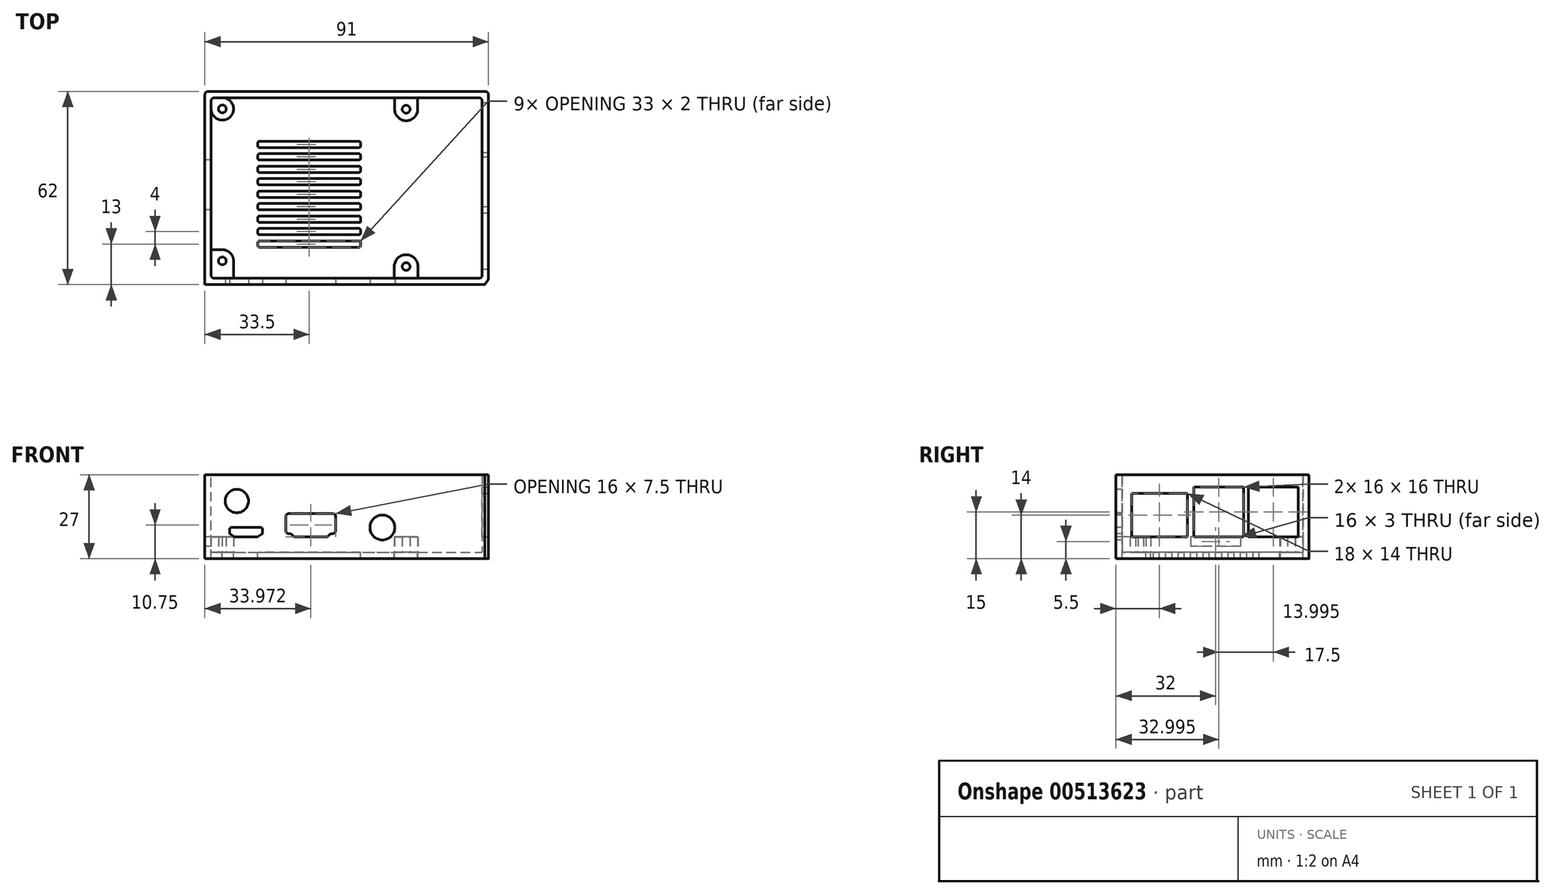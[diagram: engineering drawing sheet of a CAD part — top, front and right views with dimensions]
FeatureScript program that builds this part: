
annotation { "Feature Type Name" : "Feature", "Feature Type Description" : "" }
export const myFeature = defineFeature(function(context is Context, id is Id, definition is map)
    precondition{}
    {
        {
            var Q0;
            Q0=qCreatedBy(makeId("Top.planeOp"),FACE);
            var sketch = newSketch(context, id + "F0", { "sketchPlane" : qUnion([Q0])});
            skLineSegment(sketch, "E0.bottom", {"start": v(1, 0) * mm, "end": v(86, 0) * mm});
            skLineSegment(sketch, "E0.top", {"start": v(1, -58) * mm, "end": v(86, -58) * mm});
            skLineSegment(sketch, "E0.left", {"start": v(0, -1) * mm, "end": v(0, -57) * mm});
            skLineSegment(sketch, "E0.right", {"start": v(87, -1) * mm, "end": v(87, -57) * mm});
            skLineSegment(sketch, "E1.0", {"start": v(0, 2) * mm, "end": v(87, 2) * mm});
            skLineSegment(sketch, "E2.0", {"start": v(-2, -60) * mm, "end": v(87.8, -60) * mm});
            skLineSegment(sketch, "E3.0", {"start": v(89, 0) * mm, "end": v(89, -56.4) * mm});
            skLineSegment(sketch, "E4.0", {"start": v(-2, 0) * mm, "end": v(-2, -56) * mm});
            skLineSegment(sketch, "E5", {"start": v(0, 2) * mm, "end": v(-1, 2) * mm});
            skLineSegment(sketch, "E6", {"start": v(-2, 1) * mm, "end": v(-2, 0) * mm});
            skLineSegment(sketch, "E7", {"start": v(-2, -58) * mm, "end": v(-2, -56) * mm});
            skLineSegment(sketch, "E8", {"start": v(-2, -60) * mm, "end": v(-2, -58) * mm});
            skPoint(sketch, "E9.visualSharp", {"position": v(-2, 2) * mm});
            skArc(sketch, "E9.filletArc", {"start": v(-1, 2) * mm, "mid": v(-1.7, 1.7) * mm, "end": v(-2, 1) * mm});
            skPoint(sketch, "E10.visualSharp", {"position": v(0, 0) * mm});
            skArc(sketch, "E10.filletArc", {"start": v(1, 0) * mm, "mid": v(0.3, -0.3) * mm, "end": v(0, -1) * mm});
            skPoint(sketch, "E11.visualSharp", {"position": v(-2, -58) * mm});
            skPoint(sketch, "E12.visualSharp", {"position": v(0, -58) * mm});
            skArc(sketch, "E12.filletArc", {"start": v(0, -57) * mm, "mid": v(0.3, -57.7) * mm, "end": v(1, -58) * mm});
            skPoint(sketch, "E13.visualSharp", {"position": v(87, -58) * mm});
            skArc(sketch, "E13.filletArc", {"start": v(86, -58) * mm, "mid": v(86.7, -57.7) * mm, "end": v(87, -57) * mm});
            skPoint(sketch, "E14.visualSharp", {"position": v(87, 0) * mm});
            skArc(sketch, "E14.filletArc", {"start": v(87, -1) * mm, "mid": v(86.7, -0.3) * mm, "end": v(86, 0) * mm});
            skLineSegment(sketch, "E15", {"start": v(89, -56.4) * mm, "end": v(89, -58.06) * mm});
            skLineSegment(sketch, "E16", {"start": v(87.8, -60) * mm, "end": v(88.8, -58.66) * mm});
            skLineSegment(sketch, "E17", {"start": v(89, 0) * mm, "end": v(89, 1) * mm});
            skLineSegment(sketch, "E18", {"start": v(88, 2) * mm, "end": v(87, 2) * mm});
            skPoint(sketch, "E19.visualSharp", {"position": v(89, 2) * mm});
            skArc(sketch, "E19.filletArc", {"start": v(89, 1) * mm, "mid": v(88.7, 1.7) * mm, "end": v(88, 2) * mm});
            skPoint(sketch, "E20.visualSharp", {"position": v(89, -58.4) * mm});
            skArc(sketch, "E20.filletArc", {"start": v(88.8, -58.66) * mm, "mid": v(88.95, -58.38) * mm, "end": v(89, -58.06) * mm});
            skLineSegment(sketch, "E21.bottom", {"start": v(0, 0) * mm, "end": v(3.6, 0) * mm, "construction": true});
            skLineSegment(sketch, "E21.left", {"start": v(0, 0) * mm, "end": v(0, -3.6) * mm, "construction": true});
            skArc(sketch, "E22", {"start": v(0, -3.6) * mm, "mid": v(6.15, -6.15) * mm, "end": v(3.6, 0) * mm});
            skCircle(sketch, "E23", {"center": v(3.6, -3.6) * mm, "radius": 1.25 * mm});
            skLineSegment(sketch, "E24.bottom", {"start": v(0, -58) * mm, "end": v(3.6, -58) * mm, "construction": true});
            skLineSegment(sketch, "E24.left", {"start": v(0, -58) * mm, "end": v(0, -54.4) * mm, "construction": true});
            skLineSegment(sketch, "E25.bottom", {"start": v(15.5, -48) * mm, "end": v(47.5, -48) * mm});
            skLineSegment(sketch, "E25.top", {"start": v(15, -46) * mm, "end": v(48, -46) * mm});
            skLineSegment(sketch, "E25.left", {"start": v(15, -47.5) * mm, "end": v(15, -46.5) * mm});
            skLineSegment(sketch, "E25.right", {"start": v(48, -47.5) * mm, "end": v(48, -46.5) * mm});
            skLineSegment(sketch, "E26.bottom", {"start": v(15.5, -46) * mm, "end": v(47.5, -46) * mm});
            skLineSegment(sketch, "E26.top", {"start": v(15, -44) * mm, "end": v(48, -44) * mm});
            skLineSegment(sketch, "E27.direction1", {"start": v(15.5, -44) * mm, "end": v(40, -44) * mm, "construction": true});
            skLineSegment(sketch, "E28.bottom", {"start": v(15, -44) * mm, "end": v(47.5, -44) * mm});
            skLineSegment(sketch, "E28.top", {"start": v(15.5, -42) * mm, "end": v(47.5, -42) * mm});
            skLineSegment(sketch, "E28.left", {"start": v(15, -43.5) * mm, "end": v(15, -42.5) * mm});
            skLineSegment(sketch, "E29.bottom", {"start": v(48, -42) * mm, "end": v(15, -42) * mm});
            skLineSegment(sketch, "E29.top", {"start": v(48, -40) * mm, "end": v(15, -40) * mm});
            skLineSegment(sketch, "E30.bottom", {"start": v(15.5, -40) * mm, "end": v(47.5, -40) * mm});
            skLineSegment(sketch, "E30.top", {"start": v(15.5, -38) * mm, "end": v(47.5, -38) * mm});
            skLineSegment(sketch, "E30.left", {"start": v(15, -39.5) * mm, "end": v(15, -38.5) * mm});
            skLineSegment(sketch, "E30.right", {"start": v(48, -40) * mm, "end": v(48, -38.5) * mm});
            skLineSegment(sketch, "E31.1.0.0", {"start": v(15.5, -36) * mm, "end": v(47.5, -36) * mm});
            skLineSegment(sketch, "E31.2.0.0", {"start": v(15.5, -34) * mm, "end": v(47.5, -34) * mm});
            skLineSegment(sketch, "E31.3.0.0", {"start": v(15.5, -32) * mm, "end": v(47.5, -32) * mm});
            skLineSegment(sketch, "E31.4.0.0", {"start": v(15.5, -30) * mm, "end": v(47.5, -30) * mm});
            skLineSegment(sketch, "E31.5.0.0", {"start": v(15.5, -28) * mm, "end": v(47.5, -28) * mm});
            skLineSegment(sketch, "E31.6.0.0", {"start": v(15.5, -26) * mm, "end": v(47.5, -26) * mm});
            skLineSegment(sketch, "E31.7.0.0", {"start": v(15.5, -24) * mm, "end": v(47.5, -24) * mm});
            skLineSegment(sketch, "E31.8.0.0", {"start": v(15.5, -22) * mm, "end": v(47.5, -22) * mm});
            skLineSegment(sketch, "E31.9.0.0", {"start": v(15.5, -20) * mm, "end": v(47.5, -20) * mm});
            skLineSegment(sketch, "E31.10.0.0", {"start": v(15.5, -18) * mm, "end": v(47.5, -18) * mm});
            skLineSegment(sketch, "E31.11.0.0", {"start": v(15.5, -16) * mm, "end": v(47.5, -16) * mm});
            skLineSegment(sketch, "E31.12.0.0", {"start": v(15.5, -14) * mm, "end": v(47.5, -14) * mm});
            skLineSegment(sketch, "E32", {"start": v(15, -14.5) * mm, "end": v(15, -15.5) * mm});
            skLineSegment(sketch, "E33", {"start": v(48, -48) * mm, "end": v(48, -46) * mm});
            skPoint(sketch, "E34.visualSharp", {"position": v(15, -12) * mm});
            skPoint(sketch, "E35.newPointA", {"position": v(15, -14) * mm});
            skArc(sketch, "E35.filletArc", {"start": v(15.5, -14) * mm, "mid": v(15.15, -14.15) * mm, "end": v(15, -14.5) * mm});
            skPoint(sketch, "E36.newPointB", {"position": v(15, -16) * mm});
            skArc(sketch, "E36.filletArc", {"start": v(15, -15.5) * mm, "mid": v(15.15, -15.85) * mm, "end": v(15.5, -16) * mm});
            skLineSegment(sketch, "E37.trimOffspring", {"start": v(48, -15.5) * mm, "end": v(48, -14.5) * mm});
            skLineSegment(sketch, "E38.trimOffspring", {"start": v(48, -19.5) * mm, "end": v(48, -18.5) * mm});
            skLineSegment(sketch, "E39.trimOffspring", {"start": v(48, -23.5) * mm, "end": v(48, -22.5) * mm});
            skLineSegment(sketch, "E40.trimOffspring", {"start": v(48, -27.5) * mm, "end": v(48, -26.5) * mm});
            skLineSegment(sketch, "E41.trimOffspring", {"start": v(48, -31.5) * mm, "end": v(48, -30.5) * mm});
            skLineSegment(sketch, "E42.trimOffspring", {"start": v(48, -35.5) * mm, "end": v(48, -34.5) * mm});
            skLineSegment(sketch, "E43.trimOffspring", {"start": v(48, -39.5) * mm, "end": v(48, -38) * mm});
            skLineSegment(sketch, "E44.trimOffspring", {"start": v(48, -43.5) * mm, "end": v(48, -42.5) * mm});
            skLineSegment(sketch, "E45", {"start": v(15, -18.5) * mm, "end": v(15, -19.5) * mm});
            skLineSegment(sketch, "E46", {"start": v(15, -22.5) * mm, "end": v(15, -23.5) * mm});
            skLineSegment(sketch, "E47", {"start": v(15, -26.5) * mm, "end": v(15, -27.5) * mm});
            skLineSegment(sketch, "E48", {"start": v(15, -30.5) * mm, "end": v(15, -31.5) * mm});
            skLineSegment(sketch, "E49", {"start": v(15, -34.5) * mm, "end": v(15, -35.5) * mm});
            skPoint(sketch, "E50.visualSharp", {"position": v(15, -18) * mm});
            skArc(sketch, "E50.filletArc", {"start": v(15.5, -18) * mm, "mid": v(15.15, -18.15) * mm, "end": v(15, -18.5) * mm});
            skPoint(sketch, "E51.visualSharp", {"position": v(15, -20) * mm});
            skArc(sketch, "E51.filletArc", {"start": v(15, -19.5) * mm, "mid": v(15.15, -19.85) * mm, "end": v(15.5, -20) * mm});
            skPoint(sketch, "E52.visualSharp", {"position": v(15, -22) * mm});
            skArc(sketch, "E52.filletArc", {"start": v(15.5, -22) * mm, "mid": v(15.15, -22.15) * mm, "end": v(15, -22.5) * mm});
            skPoint(sketch, "E53.visualSharp", {"position": v(15, -24) * mm});
            skArc(sketch, "E53.filletArc", {"start": v(15, -23.5) * mm, "mid": v(15.15, -23.85) * mm, "end": v(15.5, -24) * mm});
            skPoint(sketch, "E54.visualSharp", {"position": v(15, -26) * mm});
            skArc(sketch, "E54.filletArc", {"start": v(15.5, -26) * mm, "mid": v(15.15, -26.15) * mm, "end": v(15, -26.5) * mm});
            skPoint(sketch, "E55.visualSharp", {"position": v(15, -28) * mm});
            skArc(sketch, "E55.filletArc", {"start": v(15, -27.5) * mm, "mid": v(15.15, -27.85) * mm, "end": v(15.5, -28) * mm});
            skPoint(sketch, "E56.visualSharp", {"position": v(15, -30) * mm});
            skArc(sketch, "E56.filletArc", {"start": v(15.5, -30) * mm, "mid": v(15.15, -30.15) * mm, "end": v(15, -30.5) * mm});
            skPoint(sketch, "E57.visualSharp", {"position": v(15, -32) * mm});
            skArc(sketch, "E57.filletArc", {"start": v(15, -31.5) * mm, "mid": v(15.15, -31.85) * mm, "end": v(15.5, -32) * mm});
            skPoint(sketch, "E58.visualSharp", {"position": v(15, -34) * mm});
            skArc(sketch, "E58.filletArc", {"start": v(15.5, -34) * mm, "mid": v(15.15, -34.15) * mm, "end": v(15, -34.5) * mm});
            skPoint(sketch, "E59.visualSharp", {"position": v(15, -36) * mm});
            skArc(sketch, "E59.filletArc", {"start": v(15, -35.5) * mm, "mid": v(15.15, -35.85) * mm, "end": v(15.5, -36) * mm});
            skPoint(sketch, "E60.visualSharp", {"position": v(15, -38) * mm});
            skArc(sketch, "E60.filletArc", {"start": v(15.5, -38) * mm, "mid": v(15.15, -38.15) * mm, "end": v(15, -38.5) * mm});
            skPoint(sketch, "E61.visualSharp", {"position": v(48, -18) * mm});
            skArc(sketch, "E61.filletArc", {"start": v(48, -18.5) * mm, "mid": v(47.85, -18.15) * mm, "end": v(47.5, -18) * mm});
            skPoint(sketch, "E62.visualSharp", {"position": v(48, -20) * mm});
            skArc(sketch, "E62.filletArc", {"start": v(47.5, -20) * mm, "mid": v(47.85, -19.85) * mm, "end": v(48, -19.5) * mm});
            skPoint(sketch, "E63.visualSharp", {"position": v(48, -22) * mm});
            skArc(sketch, "E63.filletArc", {"start": v(48, -22.5) * mm, "mid": v(47.85, -22.15) * mm, "end": v(47.5, -22) * mm});
            skPoint(sketch, "E64.visualSharp", {"position": v(48, -24) * mm});
            skArc(sketch, "E64.filletArc", {"start": v(47.5, -24) * mm, "mid": v(47.85, -23.85) * mm, "end": v(48, -23.5) * mm});
            skPoint(sketch, "E65.visualSharp", {"position": v(48, -26) * mm});
            skArc(sketch, "E65.filletArc", {"start": v(48, -26.5) * mm, "mid": v(47.85, -26.15) * mm, "end": v(47.5, -26) * mm});
            skPoint(sketch, "E66.visualSharp", {"position": v(48, -28) * mm});
            skArc(sketch, "E66.filletArc", {"start": v(47.5, -28) * mm, "mid": v(47.85, -27.85) * mm, "end": v(48, -27.5) * mm});
            skPoint(sketch, "E67.visualSharp", {"position": v(48, -30) * mm});
            skArc(sketch, "E67.filletArc", {"start": v(48, -30.5) * mm, "mid": v(47.85, -30.15) * mm, "end": v(47.5, -30) * mm});
            skPoint(sketch, "E68.visualSharp", {"position": v(48, -34) * mm});
            skArc(sketch, "E68.filletArc", {"start": v(48, -34.5) * mm, "mid": v(47.85, -34.15) * mm, "end": v(47.5, -34) * mm});
            skPoint(sketch, "E69.visualSharp", {"position": v(48, -32) * mm});
            skArc(sketch, "E69.filletArc", {"start": v(47.5, -32) * mm, "mid": v(47.85, -31.85) * mm, "end": v(48, -31.5) * mm});
            skPoint(sketch, "E70.visualSharp", {"position": v(48, -36) * mm});
            skArc(sketch, "E70.filletArc", {"start": v(47.5, -36) * mm, "mid": v(47.85, -35.85) * mm, "end": v(48, -35.5) * mm});
            skPoint(sketch, "E71.visualSharp", {"position": v(48, -38) * mm});
            skArc(sketch, "E71.filletArc", {"start": v(48, -38.5) * mm, "mid": v(47.85, -38.15) * mm, "end": v(47.5, -38) * mm});
            skPoint(sketch, "E72.visualSharp", {"position": v(48, -40) * mm});
            skArc(sketch, "E72.filletArc", {"start": v(47.5, -40) * mm, "mid": v(47.85, -39.85) * mm, "end": v(48, -39.5) * mm});
            skPoint(sketch, "E73.visualSharp", {"position": v(48, -42) * mm});
            skArc(sketch, "E73.filletArc", {"start": v(48, -42.5) * mm, "mid": v(47.85, -42.15) * mm, "end": v(47.5, -42) * mm});
            skPoint(sketch, "E74.visualSharp", {"position": v(48, -44) * mm});
            skArc(sketch, "E74.filletArc", {"start": v(47.5, -44) * mm, "mid": v(47.85, -43.85) * mm, "end": v(48, -43.5) * mm});
            skPoint(sketch, "E75.visualSharp", {"position": v(48, -46) * mm});
            skArc(sketch, "E75.filletArc", {"start": v(48, -46.5) * mm, "mid": v(47.85, -46.15) * mm, "end": v(47.5, -46) * mm});
            skPoint(sketch, "E76.visualSharp", {"position": v(48, -48) * mm});
            skArc(sketch, "E76.filletArc", {"start": v(47.5, -48) * mm, "mid": v(47.85, -47.85) * mm, "end": v(48, -47.5) * mm});
            skPoint(sketch, "E77.visualSharp", {"position": v(15, -46) * mm});
            skArc(sketch, "E77.filletArc", {"start": v(15.5, -46) * mm, "mid": v(15.15, -46.15) * mm, "end": v(15, -46.5) * mm});
            skPoint(sketch, "E78.visualSharp", {"position": v(15, -44) * mm});
            skArc(sketch, "E78.filletArc", {"start": v(15, -43.5) * mm, "mid": v(15.15, -43.85) * mm, "end": v(15.5, -44) * mm});
            skPoint(sketch, "E79.visualSharp", {"position": v(15, -42) * mm});
            skArc(sketch, "E79.filletArc", {"start": v(15.5, -42) * mm, "mid": v(15.15, -42.15) * mm, "end": v(15, -42.5) * mm});
            skPoint(sketch, "E80.visualSharp", {"position": v(15, -40) * mm});
            skArc(sketch, "E80.filletArc", {"start": v(15, -39.5) * mm, "mid": v(15.15, -39.85) * mm, "end": v(15.5, -40) * mm});
            skPoint(sketch, "E81.visualSharp", {"position": v(15, -48) * mm});
            skArc(sketch, "E81.filletArc", {"start": v(15, -47.5) * mm, "mid": v(15.15, -47.85) * mm, "end": v(15.5, -48) * mm});
            skPoint(sketch, "E82.visualSharp", {"position": v(48, -16) * mm});
            skArc(sketch, "E82.filletArc", {"start": v(47.5, -16) * mm, "mid": v(47.85, -15.85) * mm, "end": v(48, -15.5) * mm});
            skPoint(sketch, "E83.visualSharp", {"position": v(48, -14) * mm});
            skArc(sketch, "E83.filletArc", {"start": v(48, -14.5) * mm, "mid": v(47.85, -14.15) * mm, "end": v(47.5, -14) * mm});
            skArc(sketch, "E84", {"start": v(7.2, -52.4) * mm, "mid": v(6.1, -49.81) * mm, "end": v(3.5, -48.8) * mm});
            skCircle(sketch, "E85", {"center": v(3.6, -52.4) * mm, "radius": 1.25 * mm});
            skLineSegment(sketch, "E86", {"start": v(7.2, -52.4) * mm, "end": v(7.2, -58) * mm});
            skLineSegment(sketch, "E87", {"start": v(3.5, -48.8) * mm, "end": v(0, -48.8) * mm});
            skArc(sketch, "E88", {"start": v(66.4, -54.2) * mm, "mid": v(62.6, -50.4) * mm, "end": v(58.8, -54.2) * mm});
            skCircle(sketch, "E89", {"center": v(62.6, -54.2) * mm, "radius": 1.25 * mm});
            skArc(sketch, "E90", {"start": v(58.9, -3.7) * mm, "mid": v(62.6, -7.4) * mm, "end": v(66.3, -3.7) * mm});
            skCircle(sketch, "E91", {"center": v(62.6, -3.7) * mm, "radius": 1.25 * mm});
            skLineSegment(sketch, "E92", {"start": v(58.8, -54.2) * mm, "end": v(58.8, -58) * mm});
            skLineSegment(sketch, "E93", {"start": v(66.4, -54.2) * mm, "end": v(66.4, -58) * mm});
            skLineSegment(sketch, "E94", {"start": v(66.3, -3.7) * mm, "end": v(66.3, 0) * mm});
            skLineSegment(sketch, "E95", {"start": v(58.9, -3.7) * mm, "end": v(58.9, 0) * mm});
            skSolve(sketch);
        }
        {
            var Q0;
            Q0=makeQuery(id+"F0.imprint","IMPRINT",FACE,{"disambiguationData":[TD([[makeQuery(id+"F0.imprint","IMPRINT",EDGE,{"derivedFrom":sQuery(id+"F0.wireOp",EDGE,"E0.bottom")}),1.0]])]});
            var Q1;
            Q1=makeQuery(id+"F0.imprint","IMPRINT",FACE,{"disambiguationData":[TD([[makeQuery(id+"F0.imprint","IMPRINT",EDGE,{"derivedFrom":sQuery(id+"F0.wireOp",EDGE,"E0.bottom")}),-1.0]])]});
            extrude(context, id + "F1", {"entities" : qUnion([Q0, Q1]), "depth" : -2 * mm});
        }
        {
            var Q0;
            Q0=makeQuery(id+"F0.imprint","IMPRINT",FACE,{"disambiguationData":[TD([[makeQuery(id+"F0.imprint","IMPRINT",EDGE,{"derivedFrom":sQuery(id+"F0.wireOp",EDGE,"E0.bottom")}),1.0]])]});
            extrude(context, id + "F2", {"entities" : qUnion([Q0]), "operationType" : NewBodyOperationType.ADD, "depth" : 25 * mm});
        }
        {
            var Q0;
            {var subQ0=sQuery(id+"F0.wireOp",EDGE,"E2.0");Q0=makeQuery(id+"F2.boolean.opBoolean","MERGE",FACE,{"derivedFrom":[makeQuery(id+"F1.opExtrude","SWEPT_FACE",FACE,{"disambiguationData":[OSD([subQ0])]}),makeQuery(id+"F2.opExtrude","SWEPT_FACE",FACE,{"disambiguationData":[OSD([subQ0])]})]});}
            var sketch = newSketch(context, id + "F3", { "sketchPlane" : qUnion([Q0])});
            skLineSegment(sketch, "E96.0", {"start": v(7.62, 5) * mm, "end": v(12.82, 5) * mm});
            skLineSegment(sketch, "E97.top", {"start": v(6.47, 8) * mm, "end": v(13.97, 8) * mm});
            skLineSegment(sketch, "E97.left", {"start": v(5.97, 6.27) * mm, "end": v(5.97, 7.5) * mm});
            skLineSegment(sketch, "E98", {"start": v(7.35, 5.08) * mm, "end": v(6.2, 5.85) * mm});
            skPoint(sketch, "E99.start.orphan", {"position": v(7.47, 6) * mm});
            skPoint(sketch, "E100.visualSharp", {"position": v(5.97, 8) * mm});
            skArc(sketch, "E100.filletArc", {"start": v(6.47, 8) * mm, "mid": v(6.12, 7.85) * mm, "end": v(5.97, 7.5) * mm});
            skPoint(sketch, "E101.visualSharp", {"position": v(14.47, 8) * mm});
            skPoint(sketch, "E102.visualSharp", {"position": v(14.47, 6) * mm});
            skPoint(sketch, "E103.visualSharp", {"position": v(12.97, 5) * mm});
            skArc(sketch, "E104.filletArc", {"start": v(5.97, 6.27) * mm, "mid": v(6.03, 6.03) * mm, "end": v(6.2, 5.85) * mm});
            skArc(sketch, "E105.filletArc", {"start": v(7.35, 5.08) * mm, "mid": v(7.48, 5.02) * mm, "end": v(7.62, 5) * mm});
            skLineSegment(sketch, "E106", {"start": v(23.97, 11.18) * mm, "end": v(23.97, 6) * mm, "construction": true});
            skLineSegment(sketch, "E107.left", {"start": v(23.97, 10.5) * mm, "end": v(23.97, 7) * mm});
            skLineSegment(sketch, "E107.right", {"start": v(39.97, 10.5) * mm, "end": v(39.97, 7) * mm});
            skLineSegment(sketch, "E108.top", {"start": v(39.97, 6) * mm, "end": v(39.97, 6) * mm});
            skPoint(sketch, "E109.visualSharp", {"position": v(23.97, 11.5) * mm});
            skPoint(sketch, "E110.visualSharp", {"position": v(39.97, 11.5) * mm});
            skLineSegment(sketch, "E111.trimOffspring", {"start": v(23.97, 7.1) * mm, "end": v(23.97, 6.78) * mm, "construction": true});
            skLineSegment(sketch, "E112", {"start": v(24.97, 6) * mm, "end": v(25.24, 6) * mm});
            skLineSegment(sketch, "E113", {"start": v(25.97, 6) * mm, "end": v(25.97, 6) * mm});
            skLineSegment(sketch, "E114", {"start": v(26.97, 5) * mm, "end": v(36.97, 5) * mm});
            skLineSegment(sketch, "E115", {"start": v(37.97, 6) * mm, "end": v(37.97, 6) * mm});
            skLineSegment(sketch, "E116", {"start": v(38.7, 6) * mm, "end": v(38.97, 6) * mm});
            skPoint(sketch, "E117.visualSharp", {"position": v(23.97, 6) * mm});
            skArc(sketch, "E117.filletArc", {"start": v(23.97, 7) * mm, "mid": v(24.27, 6.3) * mm, "end": v(24.97, 6) * mm});
            skPoint(sketch, "E118.visualSharp", {"position": v(39.97, 6) * mm});
            skArc(sketch, "E118.filletArc", {"start": v(38.97, 6) * mm, "mid": v(39.68, 6.3) * mm, "end": v(39.97, 7) * mm});
            skPoint(sketch, "E119.visualSharp", {"position": v(37.97, 5) * mm});
            skArc(sketch, "E119.filletArc", {"start": v(36.97, 5) * mm, "mid": v(37.47, 5.13) * mm, "end": v(37.84, 5.5) * mm});
            skPoint(sketch, "E120.visualSharp", {"position": v(25.97, 5) * mm});
            skArc(sketch, "E120.filletArc", {"start": v(26.1, 5.5) * mm, "mid": v(26.47, 5.13) * mm, "end": v(26.97, 5) * mm});
            skPoint(sketch, "E121.visualSharp", {"position": v(37.97, 6) * mm});
            skArc(sketch, "E121.filletArc", {"start": v(38.7, 6) * mm, "mid": v(38.2, 5.87) * mm, "end": v(37.84, 5.5) * mm});
            skPoint(sketch, "E122.visualSharp", {"position": v(25.97, 6) * mm});
            skArc(sketch, "E122.filletArc", {"start": v(26.1, 5.5) * mm, "mid": v(25.74, 5.87) * mm, "end": v(25.24, 6) * mm});
            skLineSegment(sketch, "E123.0", {"start": v(8.25, -2) * mm, "end": v(8.25, 25) * mm, "construction": true});
            skCircle(sketch, "E124", {"center": v(8.25, 16.5) * mm, "radius": 3.75 * mm});
            skLineSegment(sketch, "E125.0", {"start": v(24.97, 12.5) * mm, "end": v(38.97, 12.5) * mm});
            skLineSegment(sketch, "E126", {"start": v(23.97, 11.5) * mm, "end": v(23.97, 11.5) * mm});
            skLineSegment(sketch, "E127", {"start": v(39.97, 11.5) * mm, "end": v(39.97, 10.5) * mm});
            skPoint(sketch, "E128.visualSharp", {"position": v(23.97, 12.5) * mm});
            skArc(sketch, "E128.filletArc", {"start": v(24.97, 12.5) * mm, "mid": v(24.27, 12.2) * mm, "end": v(23.97, 11.5) * mm});
            skLineSegment(sketch, "E129", {"start": v(23.97, 11.5) * mm, "end": v(23.97, 10.5) * mm});
            skPoint(sketch, "E130.visualSharp", {"position": v(39.97, 12.5) * mm});
            skArc(sketch, "E130.filletArc", {"start": v(39.97, 11.5) * mm, "mid": v(39.68, 12.2) * mm, "end": v(38.97, 12.5) * mm});
            skLineSegment(sketch, "E131", {"start": v(12.97, 5) * mm, "end": v(12.97, 5.02) * mm, "construction": true});
            skLineSegment(sketch, "E132", {"start": v(14.47, 6) * mm, "end": v(14.4, 6) * mm, "construction": true});
            skLineSegment(sketch, "E133", {"start": v(14.47, 8) * mm, "end": v(15.97, 8) * mm});
            skLineSegment(sketch, "E134", {"start": v(16.47, 7.5) * mm, "end": v(16.47, 6.27) * mm});
            skLineSegment(sketch, "E135", {"start": v(16.47, 6) * mm, "end": v(16.4, 6) * mm, "construction": true});
            skLineSegment(sketch, "E136", {"start": v(14.97, 5.02) * mm, "end": v(14.97, 5) * mm, "construction": true});
            skLineSegment(sketch, "E137", {"start": v(12.97, 5) * mm, "end": v(14.82, 5) * mm});
            skLineSegment(sketch, "E138", {"start": v(15.1, 5.08) * mm, "end": v(16.25, 5.85) * mm});
            skPoint(sketch, "E139.visualSharp", {"position": v(16.47, 8) * mm});
            skArc(sketch, "E139.filletArc", {"start": v(16.47, 7.5) * mm, "mid": v(16.33, 7.85) * mm, "end": v(15.97, 8) * mm});
            skPoint(sketch, "E140.visualSharp", {"position": v(16.47, 6) * mm});
            skArc(sketch, "E140.filletArc", {"start": v(16.25, 5.85) * mm, "mid": v(16.41, 6.03) * mm, "end": v(16.47, 6.27) * mm});
            skPoint(sketch, "E141.visualSharp", {"position": v(14.97, 5) * mm});
            skArc(sketch, "E141.filletArc", {"start": v(14.82, 5) * mm, "mid": v(14.97, 5.02) * mm, "end": v(15.1, 5.08) * mm});
            skLineSegment(sketch, "E142", {"start": v(14.47, 8) * mm, "end": v(13.97, 8) * mm});
            skCircle(sketch, "E143", {"center": v(54.97, 8) * mm, "radius": 4 * mm});
            skLineSegment(sketch, "E144", {"start": v(12.82, 5) * mm, "end": v(12.97, 5) * mm});
            skSolve(sketch);
        }
        {
            var Q0;
            {var subQ0=sQuery(id+"F0.wireOp",EDGE,"E17");var subQ1=sQuery(id+"F0.wireOp",EDGE,"E15");var subQ2=sQuery(id+"F0.wireOp",EDGE,"E3.0");Q0=makeQuery(id+"F2.boolean.opBoolean","MERGE",FACE,{"derivedFrom":[makeQuery(id+"F1.opExtrude","SWEPT_FACE",FACE,{"disambiguationData":[OSD([subQ2,subQ1,subQ0])]}),makeQuery(id+"F2.opExtrude","SWEPT_FACE",FACE,{"disambiguationData":[OSD([subQ2,subQ1,subQ0])]})]});}
            var sketch = newSketch(context, id + "F4", { "sketchPlane" : qUnion([Q0])});
            skLineSegment(sketch, "E145.bottom", {"start": v(-55, 0) * mm, "end": v(-37, 0) * mm});
            skLineSegment(sketch, "E145.left", {"start": v(-55, 5) * mm, "end": v(-55, 14) * mm});
            skLineSegment(sketch, "E145.right", {"start": v(-37, 0) * mm, "end": v(-37, 14) * mm});
            skLineSegment(sketch, "E146.top", {"start": v(-55, 19) * mm, "end": v(-37, 19) * mm});
            skLineSegment(sketch, "E146.left", {"start": v(-55, 5) * mm, "end": v(-55, 19) * mm});
            skLineSegment(sketch, "E146.right", {"start": v(-37, 5) * mm, "end": v(-37, 19) * mm});
            skLineSegment(sketch, "E147", {"start": v(-55, 5) * mm, "end": v(-37, 5) * mm});
            skLineSegment(sketch, "E148.bottom", {"start": v(-35, 5) * mm, "end": v(-19, 5) * mm});
            skLineSegment(sketch, "E148.top", {"start": v(-35, 21) * mm, "end": v(-19, 21) * mm});
            skLineSegment(sketch, "E148.left", {"start": v(-35, 5) * mm, "end": v(-35, 21) * mm});
            skLineSegment(sketch, "E148.right", {"start": v(-19, 5) * mm, "end": v(-19, 21) * mm});
            skLineSegment(sketch, "E149.bottom", {"start": v(-17.5, 5) * mm, "end": v(-1.5, 5) * mm});
            skLineSegment(sketch, "E149.top", {"start": v(-17.5, 21) * mm, "end": v(-1.5, 21) * mm});
            skLineSegment(sketch, "E149.left", {"start": v(-17.5, 5) * mm, "end": v(-17.5, 21) * mm});
            skLineSegment(sketch, "E149.right", {"start": v(-1.5, 5) * mm, "end": v(-1.5, 21) * mm});
            skSolve(sketch);
        }
        {
            var Q0;
            {var subQ4=sQuery(id+"F4.wireOp",EDGE,"E146.top");Q0=makeQuery(id+"F4.imprint","IMPRINT",FACE,{"disambiguationData":[TD([[makeQuery(id+"F4.imprint","IMPRINT",EDGE,{"derivedFrom":subQ4}),-1.0]])]});}
            var Q1;
            Q1=makeQuery(id+"F4.imprint","IMPRINT",FACE,{"disambiguationData":[TD([[makeQuery(id+"F4.imprint","IMPRINT",EDGE,{"derivedFrom":sQuery(id+"F4.wireOp",EDGE,"E148.bottom")}),1.0]])]});
            var Q2;
            Q2=makeQuery(id+"F4.imprint","IMPRINT",FACE,{"disambiguationData":[TD([[makeQuery(id+"F4.imprint","IMPRINT",EDGE,{"derivedFrom":sQuery(id+"F4.wireOp",EDGE,"E149.bottom")}),1.0]])]});
            extrude(context, id + "F5", {"entities" : qUnion([Q0, Q1, Q2]), "operationType" : NewBodyOperationType.REMOVE, "oppositeDirection" : true, "depth" : 25 * mm});
        }
        {
            var Q0;
            Q0=makeQuery(id+"F1.opExtrude","CAP_FACE",FACE,{"disambiguationData":[OSD([sQuery(id+"F0.wireOp",EDGE,"E0.bottom"),sQuery(id+"F0.wireOp",EDGE,"E0.top"),sQuery(id+"F0.wireOp",EDGE,"E0.left"),sQuery(id+"F0.wireOp",EDGE,"E1.0"),sQuery(id+"F0.wireOp",EDGE,"E2.0"),sQuery(id+"F0.wireOp",EDGE,"E3.0"),sQuery(id+"F0.wireOp",EDGE,"E4.0"),sQuery(id+"F0.wireOp",EDGE,"E5"),sQuery(id+"F0.wireOp",EDGE,"E6"),sQuery(id+"F0.wireOp",EDGE,"E7"),sQuery(id+"F0.wireOp",EDGE,"E8"),sQuery(id+"F0.wireOp",EDGE,"E9.filletArc"),sQuery(id+"F0.wireOp",EDGE,"E10.filletArc"),sQuery(id+"F0.wireOp",EDGE,"E11.filletArc"),sQuery(id+"F0.wireOp",EDGE,"E12.filletArc"),sQuery(id+"F0.wireOp",EDGE,"E15"),sQuery(id+"F0.wireOp",EDGE,"E16"),sQuery(id+"F0.wireOp",EDGE,"E17"),sQuery(id+"F0.wireOp",EDGE,"E18"),sQuery(id+"F0.wireOp",EDGE,"E19.filletArc"),sQuery(id+"F0.wireOp",EDGE,"E20.filletArc"),sQuery(id+"F0.wireOp",EDGE,"E22"),sQuery(id+"F0.wireOp",EDGE,"Xhd0Z4ac-dWOI-da8e-DmGn-wP0663GnwECI"),sQuery(id+"F0.wireOp",EDGE,"pldNfNZY-wyoh-VKPO-ICYu-ULlpv69ekvTV"),sQuery(id+"F0.wireOp",EDGE,"Ft346UMA-Ct06-alhA-WjxD-ylqalSLJ4EK5")])],"isStart":false});
            var sketch = newSketch(context, id + "F6", { "sketchPlane" : qUnion([Q0])});
            skSolve(sketch);
        }
        {
            var Q0;
            Q0=makeQuery(id+"F6.imprint","IMPRINT",FACE,{"disambiguationData":[TD([[makeQuery(id+"F6.imprint","IMPRINT",EDGE,{"derivedFrom":makeQuery(id+"F1.opExtrude","CAP_EDGE",EDGE,{"disambiguationData":[OSD([sQuery(id+"F0.wireOp",EDGE,"E0.top")])],"isStart":false})}),-1.0]])]});
            extrude(context, id + "F7", {"entities" : qUnion([Q0]), "oppositeDirection" : true, "depth" : 2 * mm});
        }
        {
            var Q0;
            {var subQ0=sQuery(id+"F0.wireOp",EDGE,"E10.filletArc");Q0=makeQuery(id+"F0.imprint","IMPRINT",FACE,{"disambiguationData":[TD([[makeQuery(id+"F0.imprint","IMPRINT",EDGE,{"derivedFrom":subQ0}),1.0]])]});}
            var Q1;
            Q1=makeQuery(id+"F0.imprint","IMPRINT",FACE,{"disambiguationData":[TD([[makeQuery(id+"F0.imprint","IMPRINT",EDGE,{"derivedFrom":sQuery(id+"F0.wireOp",EDGE,"E23")}),-1.0]])]});
            var Q2;
            Q2=makeQuery(id+"F0.imprint","IMPRINT",FACE,{"disambiguationData":[TD([[makeQuery(id+"F0.imprint","IMPRINT",EDGE,{"derivedFrom":sQuery(id+"F0.wireOp",EDGE,"E23")}),1.0]])]});
            extrude(context, id + "F8", {"entities" : qUnion([Q0, Q1, Q2]), "oppositeDirection" : true, "depth" : 2 * mm});
        }
        {
            var Q0;
            {var subQ0=sQuery(id+"F0.wireOp",EDGE,"E4.0");Q0=makeQuery(id+"F2.boolean.opBoolean","MERGE",FACE,{"derivedFrom":[makeQuery(id+"F1.opExtrude","SWEPT_FACE",FACE,{"disambiguationData":[OSD([subQ0])]}),makeQuery(id+"F2.opExtrude","SWEPT_FACE",FACE,{"disambiguationData":[OSD([subQ0])]})]});}
            var sketch = newSketch(context, id + "F9", { "sketchPlane" : qUnion([Q0])});
            skLineSegment(sketch, "E150.0", {"start": v(20, -2) * mm, "end": v(20, 25) * mm, "construction": true});
            skLineSegment(sketch, "E151.bottom", {"start": v(20, 5) * mm, "end": v(36, 5) * mm});
            skLineSegment(sketch, "E151.top", {"start": v(20, 2) * mm, "end": v(36, 2) * mm});
            skLineSegment(sketch, "E151.left", {"start": v(20, 5) * mm, "end": v(20, 2) * mm});
            skLineSegment(sketch, "E151.right", {"start": v(36, 5) * mm, "end": v(36, 2) * mm});
            skSolve(sketch);
        }
        {
            var Q0;
            Q0=makeQuery(id+"F9.imprint","IMPRINT",FACE,{"disambiguationData":[TD([[makeQuery(id+"F9.imprint","IMPRINT",EDGE,{"derivedFrom":sQuery(id+"F9.wireOp",EDGE,"E151.bottom")}),-1.0]])]});
            extrude(context, id + "F10", {"entities" : qUnion([Q0]), "operationType" : NewBodyOperationType.REMOVE, "oppositeDirection" : true, "depth" : 25 * mm});
        }
        {
            var Q0;
            Q0=makeQuery(id+"F3.imprint","IMPRINT",FACE,{"disambiguationData":[TD([[makeQuery(id+"F3.imprint","IMPRINT",EDGE,{"derivedFrom":sQuery(id+"F3.wireOp",EDGE,"E96.0")}),1.0]])]});
            var Q1;
            Q1=makeQuery(id+"F3.imprint","IMPRINT",FACE,{"disambiguationData":[TD([[makeQuery(id+"F3.imprint","IMPRINT",EDGE,{"derivedFrom":sQuery(id+"F3.wireOp",EDGE,"E124")}),1.0]])]});
            var Q2;
            Q2=makeQuery(id+"F3.imprint","IMPRINT",FACE,{"disambiguationData":[TD([[makeQuery(id+"F3.imprint","IMPRINT",EDGE,{"derivedFrom":sQuery(id+"F3.wireOp",EDGE,"E107.left")}),1.0]])]});
            var Q3;
            Q3=makeQuery(id+"F3.imprint","IMPRINT",FACE,{"disambiguationData":[TD([[makeQuery(id+"F3.imprint","IMPRINT",EDGE,{"derivedFrom":sQuery(id+"F3.wireOp",EDGE,"E143")}),1.0]])]});
            extrude(context, id + "F11", {"entities" : qUnion([Q0, Q1, Q2, Q3]), "operationType" : NewBodyOperationType.REMOVE, "oppositeDirection" : true, "depth" : 25 * mm});
        }
        {
            var Q0;
            Q0=makeQuery(id+"F0.imprint","IMPRINT",FACE,{"disambiguationData":[TD([[makeQuery(id+"F0.imprint","IMPRINT",EDGE,{"derivedFrom":sQuery(id+"F0.wireOp",EDGE,"Hv2HOEId-UtZ4-8vGZ-Q5qq-YhJOfdP6CNHn")}),-1.0]])]});
            var Q1;
            {var subQ1=sQuery(id+"F0.wireOp",EDGE,"E10.filletArc");Q1=makeQuery(id+"F0.imprint","IMPRINT",FACE,{"disambiguationData":[TD([[makeQuery(id+"F0.imprint","IMPRINT",EDGE,{"derivedFrom":subQ1}),1.0]])]});}
            var Q2;
            {var subQ1=sQuery(id+"F0.wireOp",EDGE,"E12.filletArc");Q2=makeQuery(id+"F0.imprint","IMPRINT",FACE,{"disambiguationData":[TD([[makeQuery(id+"F0.imprint","IMPRINT",EDGE,{"derivedFrom":subQ1}),1.0]])]});}
            var Q3;
            Q3=makeQuery(id+"F0.imprint","IMPRINT",FACE,{"disambiguationData":[TD([[makeQuery(id+"F0.imprint","IMPRINT",EDGE,{"derivedFrom":sQuery(id+"F0.wireOp",EDGE,"DlDQbsEE-fZNE-C9ln-6CO5-gXUED7XdOjU9")}),-1.0]])]});
            extrude(context, id + "F12", {"entities" : qUnion([Q0, Q1, Q2, Q3]), "depth" : 5 * mm});
        }
        {
            var Q0;
            Q0=makeQuery(id+"F0.imprint","IMPRINT",FACE,{"disambiguationData":[TD([[makeQuery(id+"F0.imprint","IMPRINT",EDGE,{"derivedFrom":sQuery(id+"F0.wireOp",EDGE,"E90")}),1.0]])]});
            var Q1;
            {var subQ1=sQuery(id+"F0.wireOp",EDGE,"E10.filletArc");Q1=makeQuery(id+"F0.imprint","IMPRINT",FACE,{"disambiguationData":[TD([[makeQuery(id+"F0.imprint","IMPRINT",EDGE,{"derivedFrom":subQ1}),1.0]])]});}
            var Q2;
            Q2=makeQuery(id+"F0.imprint","IMPRINT",FACE,{"disambiguationData":[TD([[makeQuery(id+"F0.imprint","IMPRINT",EDGE,{"derivedFrom":sQuery(id+"F0.wireOp",EDGE,"E88")}),1.0]])]});
            var Q3;
            {var subQ0=sQuery(id+"F0.wireOp",EDGE,"E12.filletArc");Q3=makeQuery(id+"F0.imprint","IMPRINT",FACE,{"disambiguationData":[TD([[makeQuery(id+"F0.imprint","IMPRINT",EDGE,{"derivedFrom":subQ0}),1.0]])]});}
            extrude(context, id + "F13", {"entities" : qUnion([Q0, Q1, Q2, Q3]), "depth" : 5 * mm});
        }
        {
            var Q0;
            {var subQ0=sQuery(id+"F0.wireOp",EDGE,"E12.filletArc");Q0=makeQuery(id+"F0.imprint","IMPRINT",FACE,{"disambiguationData":[TD([[makeQuery(id+"F0.imprint","IMPRINT",EDGE,{"derivedFrom":subQ0}),1.0]])]});}
            var Q1;
            Q1=makeQuery(id+"F0.imprint","IMPRINT",FACE,{"disambiguationData":[TD([[makeQuery(id+"F0.imprint","IMPRINT",EDGE,{"derivedFrom":sQuery(id+"F0.wireOp",EDGE,"E85")}),1.0]])]});
            var Q2;
            {var subQ1=sQuery(id+"F0.wireOp",EDGE,"E10.filletArc");Q2=makeQuery(id+"F0.imprint","IMPRINT",FACE,{"disambiguationData":[TD([[makeQuery(id+"F0.imprint","IMPRINT",EDGE,{"derivedFrom":subQ1}),1.0]])]});}
            var Q3;
            Q3=makeQuery(id+"F0.imprint","IMPRINT",FACE,{"disambiguationData":[TD([[makeQuery(id+"F0.imprint","IMPRINT",EDGE,{"derivedFrom":sQuery(id+"F0.wireOp",EDGE,"E23")}),1.0]])]});
            var Q4;
            Q4=makeQuery(id+"F0.imprint","IMPRINT",FACE,{"disambiguationData":[TD([[makeQuery(id+"F0.imprint","IMPRINT",EDGE,{"derivedFrom":sQuery(id+"F0.wireOp",EDGE,"E89")}),1.0]])]});
            var Q5;
            Q5=makeQuery(id+"F0.imprint","IMPRINT",FACE,{"disambiguationData":[TD([[makeQuery(id+"F0.imprint","IMPRINT",EDGE,{"derivedFrom":sQuery(id+"F0.wireOp",EDGE,"E88")}),1.0]])]});
            var Q6;
            Q6=makeQuery(id+"F0.imprint","IMPRINT",FACE,{"disambiguationData":[TD([[makeQuery(id+"F0.imprint","IMPRINT",EDGE,{"derivedFrom":sQuery(id+"F0.wireOp",EDGE,"E91")}),1.0]])]});
            var Q7;
            Q7=makeQuery(id+"F0.imprint","IMPRINT",FACE,{"disambiguationData":[TD([[makeQuery(id+"F0.imprint","IMPRINT",EDGE,{"derivedFrom":sQuery(id+"F0.wireOp",EDGE,"E90")}),1.0]])]});
            extrude(context, id + "F14", {"entities" : qUnion([Q0, Q1, Q2, Q3, Q4, Q5, Q6, Q7]), "depth" : -2 * mm});
        }
    });
